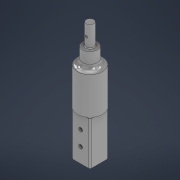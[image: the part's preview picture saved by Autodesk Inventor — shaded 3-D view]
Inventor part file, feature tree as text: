
AUTODESK INVENTOR PART (.ipt)
format: ipt  version: 2021 (Build 250183000, 183)  size: 258,560 bytes
history: native  units: mm
features: sketch x7, extrude x4, fillet x4, plane x2, hole x2
ambient origin geometry x8: Origin, YZ Plane, XZ Plane, XY Plane, X Axis, Y Axis, Z Axis, Center Point
bodies: Solid1 (feature_tree)
feature tree (19):
  extrude  "Extrusion1"  Depth=25.0mm
  fillet  "Fillet1"  Radius=12.5mm
  extrude  "Extrusion2"  Depth=2.5mm
  sketch  "Sketch3"  dims[d5=60.0mm d6=0.0mm d7=2.0mm]
  extrude  "Extrusion3"  Depth=2.0mm
  plane  "Work Plane1"
  hole  "Hole1"  [1 undecoded]
  plane  "Work Plane2"
  extrude  "Extrusion4"  Depth=10.0mm TaperAngle=0.0deg
  fillet  "Fillet3"  Radius=12.5mm
  fillet  "Fillet4"  Radius=15.0mm
  hole  "Hole2"  [1 undecoded]
  fillet  "Fillet5"  Radius=10.0mm
  sketch  "Sketch1"  dims[d0=25.0mm d1=25.0mm d2=12.5mm]
  sketch  "Sketch2"  dims[d3=12.5mm d4=2.5mm]
  sketch  "Sketch4"  dims[d8=33.941125mm d9=50.0mm d10=0.0mm]
  sketch  "Sketch5"  dims[d11=10.0mm d12=50.0mm d13=0.0mm d19=12.5mm]
  sketch  "Sketch6"  dims[d20=3.242mm d21=8.0mm d22=4.0mm d23=2.0mm d24=90.0deg d25=8.0mm d26=0.0mm d28=15.0mm]
  sketch  "Sketch7"  dims[d29=-28.0mm d30=5.0mm d31=10.0mm d32=0.0mm d33=1.0mm d34=7.0mm d35=0.0mm d36=0.0mm d37=20.0mm d38=20.0mm d39=5.0mm d40=6.0mm d41=4.0mm d42=2.0mm d43=90.0deg d44=8.0mm d45=20.594885mm d46=2.0mm]
note: 2 required parameter values undecoded (feature->parameter linkage not recoverable at this tier; creation-order binding heuristic only, values carry confidence <= 0.55)
